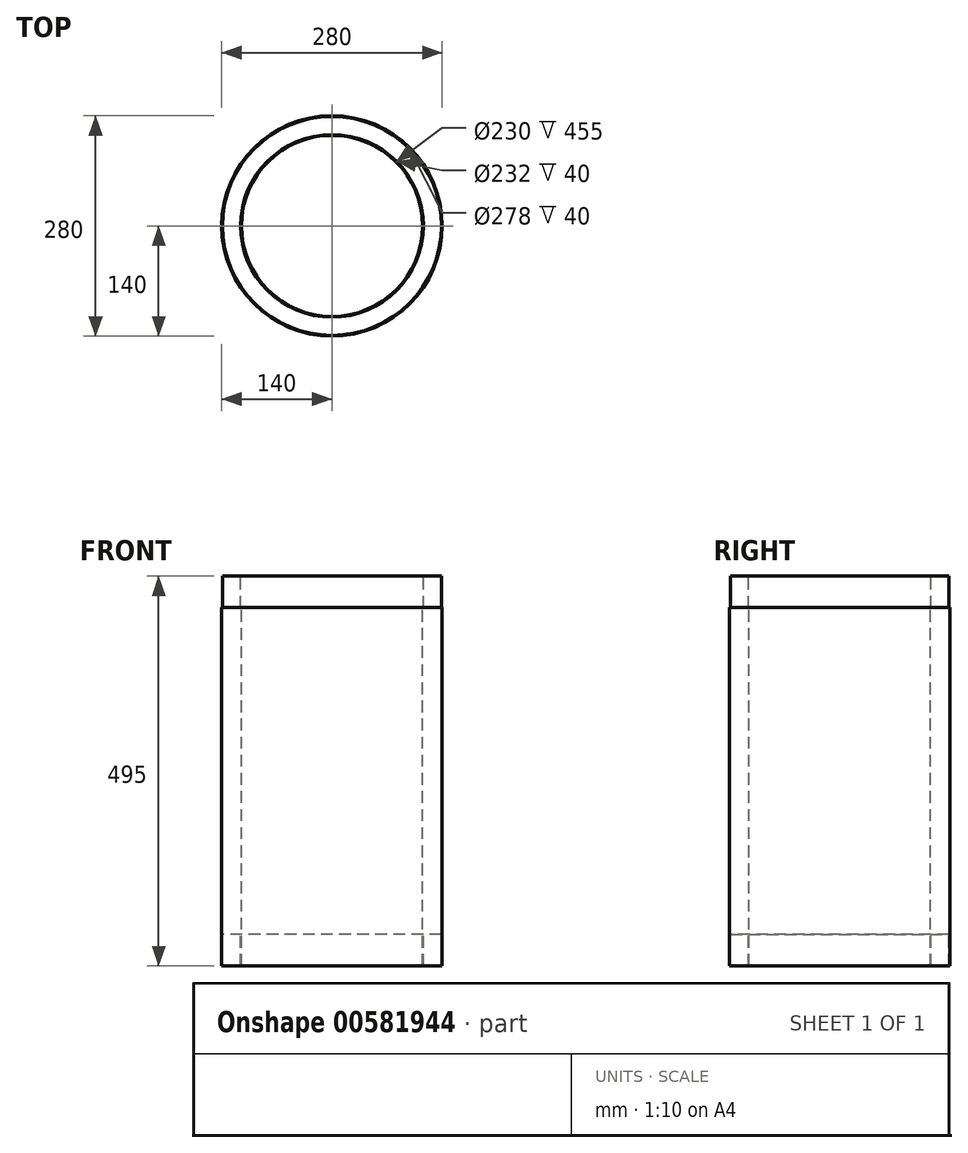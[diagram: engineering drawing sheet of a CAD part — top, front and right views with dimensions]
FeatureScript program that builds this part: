
annotation { "Feature Type Name" : "Feature", "Feature Type Description" : "" }
export const myFeature = defineFeature(function(context is Context, id is Id, definition is map)
    precondition{}
    {
        {
            var Q0;
            Q0=qCreatedBy(makeId("Front.planeOp"),FACE);
            var sketch = newSketch(context, id + "F0", { "sketchPlane" : qUnion([Q0])});
            skLineSegment(sketch, "E0", {"start": v(0, 345.75) * mm, "end": v(0, -558.03) * mm, "construction": true});
            skLineSegment(sketch, "E1", {"start": v(-115, -518.84) * mm, "end": v(-115, -63.84) * mm});
            skLineSegment(sketch, "E2", {"start": v(-115, -63.84) * mm, "end": v(-116, -63.84) * mm});
            skLineSegment(sketch, "E3", {"start": v(-116, -63.84) * mm, "end": v(-116, -23.84) * mm});
            skLineSegment(sketch, "E4", {"start": v(-116, -23.84) * mm, "end": v(-139, -23.84) * mm});
            skLineSegment(sketch, "E5", {"start": v(-139, -23.84) * mm, "end": v(-139, -63.84) * mm});
            skLineSegment(sketch, "E6", {"start": v(-139, -63.84) * mm, "end": v(-140, -63.84) * mm});
            skLineSegment(sketch, "E7", {"start": v(-140, -63.84) * mm, "end": v(-140, -518.84) * mm});
            skLineSegment(sketch, "E8", {"start": v(-140, -518.84) * mm, "end": v(-139, -518.84) * mm});
            skLineSegment(sketch, "E9", {"start": v(-139, -518.84) * mm, "end": v(-139, -478.84) * mm});
            skLineSegment(sketch, "E10", {"start": v(-139, -478.84) * mm, "end": v(-116, -478.84) * mm});
            skLineSegment(sketch, "E11", {"start": v(-116, -478.84) * mm, "end": v(-116, -518.84) * mm});
            skLineSegment(sketch, "E12", {"start": v(-116, -518.84) * mm, "end": v(-115, -518.84) * mm});
            skSolve(sketch);
        }
        {
            var Q0;
            Q0=qSketchRegion(id+"F0",true);
            var Q1;
            Q1=sQuery(id+"F0.wireOp",EDGE,"E0");
            revolve(context, id + "F1", {"entities" : qUnion([Q0]), "axis" : qUnion([Q1]), "revolveType" : RevolveType.FULL});
        }
    });
